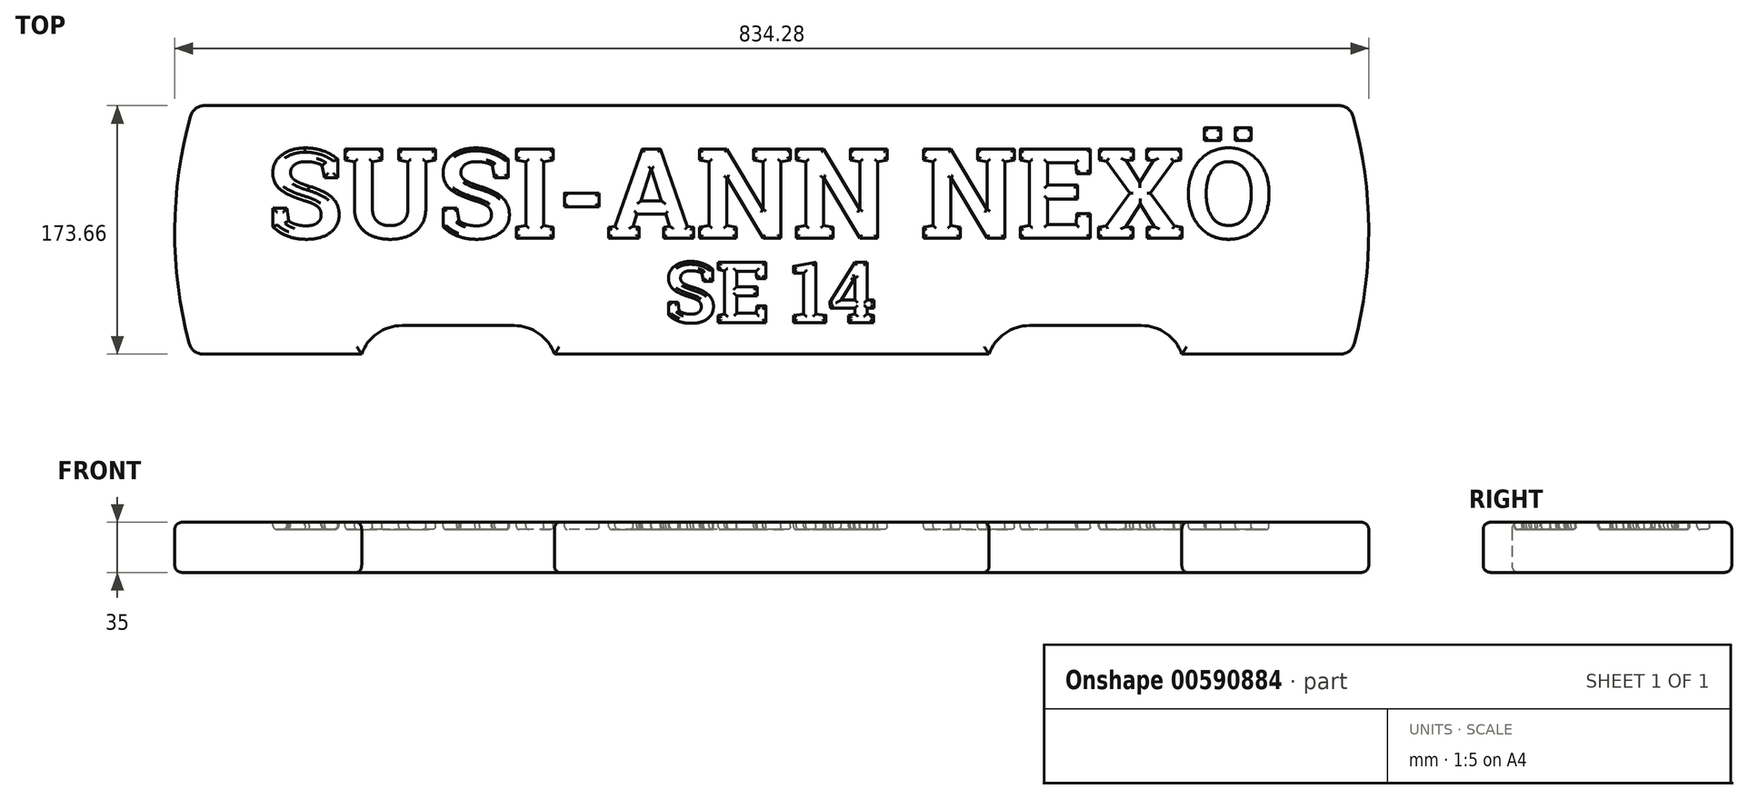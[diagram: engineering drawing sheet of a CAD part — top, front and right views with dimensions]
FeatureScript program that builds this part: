
annotation { "Feature Type Name" : "Feature", "Feature Type Description" : "" }
export const myFeature = defineFeature(function(context is Context, id is Id, definition is map)
    precondition{}
    {
        {
            var Q0;
            Q0=qCreatedBy(makeId("Top.planeOp"),FACE);
            var sketch = newSketch(context, id + "F0", { "sketchPlane" : qUnion([Q0])});
            skLineSegment(sketch, "E0.bottom", {"start": v(7.6, 0) * mm, "end": v(118.46, 0) * mm});
            skLineSegment(sketch, "E0.top", {"start": v(8.6, 173.66) * mm, "end": v(801.4, 173.66) * mm});
            skArc(sketch, "E1", {"start": v(-1.04, 166.34) * mm, "mid": v(-12.13, 86.96) * mm, "end": v(-2.07, 7.45) * mm});
            skLineSegment(sketch, "E2", {"start": v(405, 173.66) * mm, "end": v(405, 0) * mm, "construction": true});
            skArc(sketch, "E3.MirrorCS", {"start": v(811.04, 166.34) * mm, "mid": v(822.13, 86.96) * mm, "end": v(812.07, 7.45) * mm});
            skPoint(sketch, "E4.visualSharp", {"position": v(1.1, 173.66) * mm});
            skArc(sketch, "E4.filletArc", {"start": v(8.6, 173.66) * mm, "mid": v(2.54, 171.62) * mm, "end": v(-1.04, 166.34) * mm});
            skArc(sketch, "E5.MirrorCS", {"start": v(801.4, 173.66) * mm, "mid": v(807.46, 171.62) * mm, "end": v(811.04, 166.34) * mm});
            skPoint(sketch, "E6.orphan", {"position": v(808.9, 173.66) * mm});
            skLineSegment(sketch, "E7", {"start": v(-12.13, 86.9) * mm, "end": v(822.13, 86.9) * mm, "construction": true});
            skPoint(sketch, "E7.startSnap0", {"position": v(-12.13, 83.1) * mm});
            skPoint(sketch, "E8.visualSharp", {"position": v(0, 0) * mm});
            skArc(sketch, "E8.filletArc", {"start": v(-2.07, 7.45) * mm, "mid": v(1.5, 2.08) * mm, "end": v(7.6, 0) * mm});
            skPoint(sketch, "E9.visualSharp", {"position": v(810, 0) * mm});
            skArc(sketch, "E9.filletArc", {"start": v(802.4, 0) * mm, "mid": v(808.5, 2.08) * mm, "end": v(812.07, 7.45) * mm});
            skLineSegment(sketch, "E10.top", {"start": v(146.74, 20) * mm, "end": v(224.83, 20) * mm});
            skPoint(sketch, "E11.visualSharp", {"position": v(126.74, 20) * mm});
            skArc(sketch, "E11.filletArc", {"start": v(146.74, 20) * mm, "mid": v(129.42, 14.5) * mm, "end": v(118.46, 0) * mm});
            skPoint(sketch, "E12.visualSharp", {"position": v(244.83, 20) * mm});
            skArc(sketch, "E12.filletArc", {"start": v(253.12, 0) * mm, "mid": v(242.16, 14.5) * mm, "end": v(224.83, 20) * mm});
            skLineSegment(sketch, "E13.trimOffspring", {"start": v(253.12, 0) * mm, "end": v(556.88, 0) * mm});
            skArc(sketch, "E14.MirrorCS", {"start": v(556.88, 0) * mm, "mid": v(567.84, 14.5) * mm, "end": v(585.17, 20) * mm});
            skArc(sketch, "E15.MirrorCS", {"start": v(663.26, 20) * mm, "mid": v(680.58, 14.5) * mm, "end": v(691.54, 0) * mm});
            skPoint(sketch, "E16.MirrorP", {"position": v(565.17, 20) * mm});
            skPoint(sketch, "E17.MirrorP", {"position": v(683.26, 20) * mm});
            skLineSegment(sketch, "E18.MirrorCS", {"start": v(663.26, 20) * mm, "end": v(585.17, 20) * mm});
            skLineSegment(sketch, "E19.trimOffspring", {"start": v(691.54, 0) * mm, "end": v(802.4, 0) * mm});
            skSolve(sketch);
        }
        {
            var Q0;
            Q0 = qSketchRegion(id + "F0", true);
            extrude(context, id + "F1", {"entities" : qUnion([Q0]), "depth" : 35 * mm, "offsetDistance" : 25 * mm});
        }
        {
            var Q0;
            Q0=makeQuery(id+"F1.opExtrude","CAP_FACE",FACE,{"disambiguationData":[OSD([sQuery(id+"F0.wireOp",EDGE,"E0.bottom"),sQuery(id+"F0.wireOp",EDGE,"E0.top"),sQuery(id+"F0.wireOp",EDGE,"E1"),sQuery(id+"F0.wireOp",EDGE,"E3.MirrorCS"),sQuery(id+"F0.wireOp",EDGE,"E4.filletArc"),sQuery(id+"F0.wireOp",EDGE,"E5.MirrorCS"),sQuery(id+"F0.wireOp",EDGE,"E8.filletArc"),sQuery(id+"F0.wireOp",EDGE,"E9.filletArc"),sQuery(id+"F0.wireOp",EDGE,"E10.top"),sQuery(id+"F0.wireOp",EDGE,"E11.filletArc"),sQuery(id+"F0.wireOp",EDGE,"E12.filletArc"),sQuery(id+"F0.wireOp",EDGE,"E13.trimOffspring"),sQuery(id+"F0.wireOp",EDGE,"E14.MirrorCS"),sQuery(id+"F0.wireOp",EDGE,"E15.MirrorCS"),sQuery(id+"F0.wireOp",EDGE,"E18.MirrorCS"),sQuery(id+"F0.wireOp",EDGE,"E19.trimOffspring")])],"isStart":false});
            var Q1;
            Q1=makeQuery(id+"F1.opExtrude","CAP_FACE",FACE,{"disambiguationData":[OSD([sQuery(id+"F0.wireOp",EDGE,"E0.bottom"),sQuery(id+"F0.wireOp",EDGE,"E0.top"),sQuery(id+"F0.wireOp",EDGE,"E1"),sQuery(id+"F0.wireOp",EDGE,"E3.MirrorCS"),sQuery(id+"F0.wireOp",EDGE,"E4.filletArc"),sQuery(id+"F0.wireOp",EDGE,"E5.MirrorCS"),sQuery(id+"F0.wireOp",EDGE,"E8.filletArc"),sQuery(id+"F0.wireOp",EDGE,"E9.filletArc"),sQuery(id+"F0.wireOp",EDGE,"E10.top"),sQuery(id+"F0.wireOp",EDGE,"E11.filletArc"),sQuery(id+"F0.wireOp",EDGE,"E12.filletArc"),sQuery(id+"F0.wireOp",EDGE,"E13.trimOffspring"),sQuery(id+"F0.wireOp",EDGE,"E14.MirrorCS"),sQuery(id+"F0.wireOp",EDGE,"E15.MirrorCS"),sQuery(id+"F0.wireOp",EDGE,"E18.MirrorCS"),sQuery(id+"F0.wireOp",EDGE,"E19.trimOffspring")])],"isStart":true});
            fillet(context, id + "F2", {"entities" : qUnion([Q0, Q1]), "radius" : 5 * mm, "tangentPropagation" : true, "allowEdgeOverflow" : false});
        }
        {
            var Q0;
            Q0=makeQuery(id+"F1.opExtrude","CAP_FACE",FACE,{"disambiguationData":[OSD([sQuery(id+"F0.wireOp",EDGE,"E0.bottom"),sQuery(id+"F0.wireOp",EDGE,"E0.top"),sQuery(id+"F0.wireOp",EDGE,"E1"),sQuery(id+"F0.wireOp",EDGE,"E3.MirrorCS"),sQuery(id+"F0.wireOp",EDGE,"E4.filletArc"),sQuery(id+"F0.wireOp",EDGE,"E5.MirrorCS"),sQuery(id+"F0.wireOp",EDGE,"E8.filletArc"),sQuery(id+"F0.wireOp",EDGE,"E9.filletArc"),sQuery(id+"F0.wireOp",EDGE,"E10.top"),sQuery(id+"F0.wireOp",EDGE,"E11.filletArc"),sQuery(id+"F0.wireOp",EDGE,"E12.filletArc"),sQuery(id+"F0.wireOp",EDGE,"E13.trimOffspring"),sQuery(id+"F0.wireOp",EDGE,"E14.MirrorCS"),sQuery(id+"F0.wireOp",EDGE,"E15.MirrorCS"),sQuery(id+"F0.wireOp",EDGE,"E18.MirrorCS"),sQuery(id+"F0.wireOp",EDGE,"E19.trimOffspring")])],"isStart":false});
            var sketch = newSketch(context, id + "F3", { "sketchPlane" : qUnion([Q0])});
            skText(sketch, "E20", { "text": "SUSI-ANN NEXÖ", "fontName": "RobotoSlab-Bold.ttf"});
            skLineSegment(sketch, "E21", {"start": v(405, 168.66) * mm, "end": v(405, 5) * mm, "construction": true});
            skText(sketch, "E22", { "text": "SE 14", "fontName": "RobotoSlab-Bold.ttf"});
            const initialGuessF3  = {"E20": [0.05221, 0.08113, 1, 0, 0.06292], "E22": [0.33004, 0.02212, 1, 0, 0.04265]};
            skSetInitialGuess(sketch, initialGuessF3);
            skSolve(sketch);
        }
        {
            var Q0;
            Q0 = qSketchRegion(id + "F3", true);
            extrude(context, id + "F4", {"entities" : qUnion([Q0]), "operationType" : NewBodyOperationType.REMOVE, "oppositeDirection" : true, "depth" : 5 * mm, "offsetDistance" : 25 * mm});
        }
        {
            var Q0;
            Q0=makeQuery(id+"F4.boolean.opBoolean","COPY",FACE,{"derivedFrom":makeQuery(id+"F4.opExtrude","CAP_FACE",FACE,{"disambiguationData":[OSD([sQuery(id+"F3.wireOp",EDGE,"E20.sketch_text.stroke-0"),sQuery(id+"F3.wireOp",EDGE,"E20.sketch_text.stroke-1"),sQuery(id+"F3.wireOp",EDGE,"E20.sketch_text.stroke-2"),sQuery(id+"F3.wireOp",EDGE,"E20.sketch_text.stroke-3"),sQuery(id+"F3.wireOp",EDGE,"E20.sketch_text.stroke-4"),sQuery(id+"F3.wireOp",EDGE,"E20.sketch_text.stroke-5"),sQuery(id+"F3.wireOp",EDGE,"E20.sketch_text.stroke-6"),sQuery(id+"F3.wireOp",EDGE,"E20.sketch_text.stroke-7"),sQuery(id+"F3.wireOp",EDGE,"E20.sketch_text.stroke-8"),sQuery(id+"F3.wireOp",EDGE,"E20.sketch_text.stroke-9"),sQuery(id+"F3.wireOp",EDGE,"E20.sketch_text.stroke-10"),sQuery(id+"F3.wireOp",EDGE,"E20.sketch_text.stroke-11"),sQuery(id+"F3.wireOp",EDGE,"E20.sketch_text.stroke-12"),sQuery(id+"F3.wireOp",EDGE,"E20.sketch_text.stroke-13"),sQuery(id+"F3.wireOp",EDGE,"E20.sketch_text.stroke-14"),sQuery(id+"F3.wireOp",EDGE,"E20.sketch_text.stroke-15"),sQuery(id+"F3.wireOp",EDGE,"E20.sketch_text.stroke-16"),sQuery(id+"F3.wireOp",EDGE,"E20.sketch_text.stroke-17"),sQuery(id+"F3.wireOp",EDGE,"E20.sketch_text.stroke-18"),sQuery(id+"F3.wireOp",EDGE,"E20.sketch_text.stroke-19"),sQuery(id+"F3.wireOp",EDGE,"E20.sketch_text.stroke-20"),sQuery(id+"F3.wireOp",EDGE,"E20.sketch_text.stroke-21"),sQuery(id+"F3.wireOp",EDGE,"E20.sketch_text.stroke-22"),sQuery(id+"F3.wireOp",EDGE,"E20.sketch_text.stroke-23"),sQuery(id+"F3.wireOp",EDGE,"E20.sketch_text.stroke-24"),sQuery(id+"F3.wireOp",EDGE,"E20.sketch_text.stroke-25"),sQuery(id+"F3.wireOp",EDGE,"E20.sketch_text.stroke-26"),sQuery(id+"F3.wireOp",EDGE,"E20.sketch_text.stroke-27"),sQuery(id+"F3.wireOp",EDGE,"E20.sketch_text.stroke-28"),sQuery(id+"F3.wireOp",EDGE,"E20.sketch_text.stroke-29")])],"isStart":false})});
            fillet(context, id + "F5", {"entities" : qUnion([Q0]), "radius" : 3 * mm, "tangentPropagation" : true, "allowEdgeOverflow" : false});
        }
        {
            var Q0;
            Q0=makeQuery(id+"F4.boolean.opBoolean","COPY",FACE,{"derivedFrom":makeQuery(id+"F4.opExtrude","CAP_FACE",FACE,{"disambiguationData":[OSD([sQuery(id+"F3.wireOp",EDGE,"E20.sketch_text.stroke-30"),sQuery(id+"F3.wireOp",EDGE,"E20.sketch_text.stroke-31"),sQuery(id+"F3.wireOp",EDGE,"E20.sketch_text.stroke-32"),sQuery(id+"F3.wireOp",EDGE,"E20.sketch_text.stroke-33"),sQuery(id+"F3.wireOp",EDGE,"E20.sketch_text.stroke-34"),sQuery(id+"F3.wireOp",EDGE,"E20.sketch_text.stroke-35"),sQuery(id+"F3.wireOp",EDGE,"E20.sketch_text.stroke-36"),sQuery(id+"F3.wireOp",EDGE,"E20.sketch_text.stroke-37"),sQuery(id+"F3.wireOp",EDGE,"E20.sketch_text.stroke-38"),sQuery(id+"F3.wireOp",EDGE,"E20.sketch_text.stroke-39"),sQuery(id+"F3.wireOp",EDGE,"E20.sketch_text.stroke-40"),sQuery(id+"F3.wireOp",EDGE,"E20.sketch_text.stroke-41"),sQuery(id+"F3.wireOp",EDGE,"E20.sketch_text.stroke-42"),sQuery(id+"F3.wireOp",EDGE,"E20.sketch_text.stroke-43"),sQuery(id+"F3.wireOp",EDGE,"E20.sketch_text.stroke-44"),sQuery(id+"F3.wireOp",EDGE,"E20.sketch_text.stroke-45"),sQuery(id+"F3.wireOp",EDGE,"E20.sketch_text.stroke-46"),sQuery(id+"F3.wireOp",EDGE,"E20.sketch_text.stroke-47"),sQuery(id+"F3.wireOp",EDGE,"E20.sketch_text.stroke-48"),sQuery(id+"F3.wireOp",EDGE,"E20.sketch_text.stroke-49"),sQuery(id+"F3.wireOp",EDGE,"E20.sketch_text.stroke-50"),sQuery(id+"F3.wireOp",EDGE,"E20.sketch_text.stroke-51"),sQuery(id+"F3.wireOp",EDGE,"E20.sketch_text.stroke-52"),sQuery(id+"F3.wireOp",EDGE,"E20.sketch_text.stroke-53")])],"isStart":false})});
            var Q1;
            Q1=makeQuery(id+"F4.boolean.opBoolean","COPY",FACE,{"derivedFrom":makeQuery(id+"F4.opExtrude","CAP_FACE",FACE,{"disambiguationData":[OSD([sQuery(id+"F3.wireOp",EDGE,"E20.sketch_text.stroke-54"),sQuery(id+"F3.wireOp",EDGE,"E20.sketch_text.stroke-55"),sQuery(id+"F3.wireOp",EDGE,"E20.sketch_text.stroke-56"),sQuery(id+"F3.wireOp",EDGE,"E20.sketch_text.stroke-57"),sQuery(id+"F3.wireOp",EDGE,"E20.sketch_text.stroke-58"),sQuery(id+"F3.wireOp",EDGE,"E20.sketch_text.stroke-59"),sQuery(id+"F3.wireOp",EDGE,"E20.sketch_text.stroke-60"),sQuery(id+"F3.wireOp",EDGE,"E20.sketch_text.stroke-61"),sQuery(id+"F3.wireOp",EDGE,"E20.sketch_text.stroke-62"),sQuery(id+"F3.wireOp",EDGE,"E20.sketch_text.stroke-63"),sQuery(id+"F3.wireOp",EDGE,"E20.sketch_text.stroke-64"),sQuery(id+"F3.wireOp",EDGE,"E20.sketch_text.stroke-65"),sQuery(id+"F3.wireOp",EDGE,"E20.sketch_text.stroke-66"),sQuery(id+"F3.wireOp",EDGE,"E20.sketch_text.stroke-67"),sQuery(id+"F3.wireOp",EDGE,"E20.sketch_text.stroke-68"),sQuery(id+"F3.wireOp",EDGE,"E20.sketch_text.stroke-69"),sQuery(id+"F3.wireOp",EDGE,"E20.sketch_text.stroke-70"),sQuery(id+"F3.wireOp",EDGE,"E20.sketch_text.stroke-71"),sQuery(id+"F3.wireOp",EDGE,"E20.sketch_text.stroke-72"),sQuery(id+"F3.wireOp",EDGE,"E20.sketch_text.stroke-73"),sQuery(id+"F3.wireOp",EDGE,"E20.sketch_text.stroke-74"),sQuery(id+"F3.wireOp",EDGE,"E20.sketch_text.stroke-75"),sQuery(id+"F3.wireOp",EDGE,"E20.sketch_text.stroke-76"),sQuery(id+"F3.wireOp",EDGE,"E20.sketch_text.stroke-77"),sQuery(id+"F3.wireOp",EDGE,"E20.sketch_text.stroke-78"),sQuery(id+"F3.wireOp",EDGE,"E20.sketch_text.stroke-79"),sQuery(id+"F3.wireOp",EDGE,"E20.sketch_text.stroke-80"),sQuery(id+"F3.wireOp",EDGE,"E20.sketch_text.stroke-81"),sQuery(id+"F3.wireOp",EDGE,"E20.sketch_text.stroke-82"),sQuery(id+"F3.wireOp",EDGE,"E20.sketch_text.stroke-83")])],"isStart":false})});
            var Q2;
            Q2=makeQuery(id+"F4.boolean.opBoolean","COPY",FACE,{"derivedFrom":makeQuery(id+"F4.opExtrude","CAP_FACE",FACE,{"disambiguationData":[OSD([sQuery(id+"F3.wireOp",EDGE,"E20.sketch_text.stroke-84"),sQuery(id+"F3.wireOp",EDGE,"E20.sketch_text.stroke-85"),sQuery(id+"F3.wireOp",EDGE,"E20.sketch_text.stroke-86"),sQuery(id+"F3.wireOp",EDGE,"E20.sketch_text.stroke-87"),sQuery(id+"F3.wireOp",EDGE,"E20.sketch_text.stroke-88"),sQuery(id+"F3.wireOp",EDGE,"E20.sketch_text.stroke-89"),sQuery(id+"F3.wireOp",EDGE,"E20.sketch_text.stroke-90"),sQuery(id+"F3.wireOp",EDGE,"E20.sketch_text.stroke-91"),sQuery(id+"F3.wireOp",EDGE,"E20.sketch_text.stroke-92"),sQuery(id+"F3.wireOp",EDGE,"E20.sketch_text.stroke-93"),sQuery(id+"F3.wireOp",EDGE,"E20.sketch_text.stroke-94"),sQuery(id+"F3.wireOp",EDGE,"E20.sketch_text.stroke-95")])],"isStart":false})});
            var Q3;
            Q3=makeQuery(id+"F4.boolean.opBoolean","COPY",FACE,{"derivedFrom":makeQuery(id+"F4.opExtrude","CAP_FACE",FACE,{"disambiguationData":[OSD([sQuery(id+"F3.wireOp",EDGE,"E20.sketch_text.stroke-96"),sQuery(id+"F3.wireOp",EDGE,"E20.sketch_text.stroke-97"),sQuery(id+"F3.wireOp",EDGE,"E20.sketch_text.stroke-98"),sQuery(id+"F3.wireOp",EDGE,"E20.sketch_text.stroke-99")])],"isStart":false})});
            var Q4;
            Q4=makeQuery(id+"F4.boolean.opBoolean","COPY",FACE,{"derivedFrom":makeQuery(id+"F4.opExtrude","CAP_FACE",FACE,{"disambiguationData":[OSD([sQuery(id+"F3.wireOp",EDGE,"E20.sketch_text.stroke-100"),sQuery(id+"F3.wireOp",EDGE,"E20.sketch_text.stroke-101"),sQuery(id+"F3.wireOp",EDGE,"E20.sketch_text.stroke-102"),sQuery(id+"F3.wireOp",EDGE,"E20.sketch_text.stroke-103"),sQuery(id+"F3.wireOp",EDGE,"E20.sketch_text.stroke-104"),sQuery(id+"F3.wireOp",EDGE,"E20.sketch_text.stroke-105"),sQuery(id+"F3.wireOp",EDGE,"E20.sketch_text.stroke-106"),sQuery(id+"F3.wireOp",EDGE,"E20.sketch_text.stroke-107"),sQuery(id+"F3.wireOp",EDGE,"E20.sketch_text.stroke-108"),sQuery(id+"F3.wireOp",EDGE,"E20.sketch_text.stroke-109"),sQuery(id+"F3.wireOp",EDGE,"E20.sketch_text.stroke-110"),sQuery(id+"F3.wireOp",EDGE,"E20.sketch_text.stroke-111"),sQuery(id+"F3.wireOp",EDGE,"E20.sketch_text.stroke-112"),sQuery(id+"F3.wireOp",EDGE,"E20.sketch_text.stroke-113"),sQuery(id+"F3.wireOp",EDGE,"E20.sketch_text.stroke-114"),sQuery(id+"F3.wireOp",EDGE,"E20.sketch_text.stroke-115"),sQuery(id+"F3.wireOp",EDGE,"E20.sketch_text.stroke-116"),sQuery(id+"F3.wireOp",EDGE,"E20.sketch_text.stroke-117"),sQuery(id+"F3.wireOp",EDGE,"E20.sketch_text.stroke-118"),sQuery(id+"F3.wireOp",EDGE,"E20.sketch_text.stroke-119")])],"isStart":false})});
            var Q5;
            Q5=makeQuery(id+"F4.boolean.opBoolean","COPY",FACE,{"derivedFrom":makeQuery(id+"F4.opExtrude","CAP_FACE",FACE,{"disambiguationData":[OSD([sQuery(id+"F3.wireOp",EDGE,"E20.sketch_text.stroke-120"),sQuery(id+"F3.wireOp",EDGE,"E20.sketch_text.stroke-121"),sQuery(id+"F3.wireOp",EDGE,"E20.sketch_text.stroke-122"),sQuery(id+"F3.wireOp",EDGE,"E20.sketch_text.stroke-123"),sQuery(id+"F3.wireOp",EDGE,"E20.sketch_text.stroke-124"),sQuery(id+"F3.wireOp",EDGE,"E20.sketch_text.stroke-125"),sQuery(id+"F3.wireOp",EDGE,"E20.sketch_text.stroke-126"),sQuery(id+"F3.wireOp",EDGE,"E20.sketch_text.stroke-127"),sQuery(id+"F3.wireOp",EDGE,"E20.sketch_text.stroke-128"),sQuery(id+"F3.wireOp",EDGE,"E20.sketch_text.stroke-129"),sQuery(id+"F3.wireOp",EDGE,"E20.sketch_text.stroke-130"),sQuery(id+"F3.wireOp",EDGE,"E20.sketch_text.stroke-131"),sQuery(id+"F3.wireOp",EDGE,"E20.sketch_text.stroke-132"),sQuery(id+"F3.wireOp",EDGE,"E20.sketch_text.stroke-133"),sQuery(id+"F3.wireOp",EDGE,"E20.sketch_text.stroke-134"),sQuery(id+"F3.wireOp",EDGE,"E20.sketch_text.stroke-135"),sQuery(id+"F3.wireOp",EDGE,"E20.sketch_text.stroke-136"),sQuery(id+"F3.wireOp",EDGE,"E20.sketch_text.stroke-137"),sQuery(id+"F3.wireOp",EDGE,"E20.sketch_text.stroke-138"),sQuery(id+"F3.wireOp",EDGE,"E20.sketch_text.stroke-139"),sQuery(id+"F3.wireOp",EDGE,"E20.sketch_text.stroke-140"),sQuery(id+"F3.wireOp",EDGE,"E20.sketch_text.stroke-141"),sQuery(id+"F3.wireOp",EDGE,"E20.sketch_text.stroke-142"),sQuery(id+"F3.wireOp",EDGE,"E20.sketch_text.stroke-143")])],"isStart":false})});
            var Q6;
            Q6=makeQuery(id+"F4.boolean.opBoolean","COPY",FACE,{"derivedFrom":makeQuery(id+"F4.opExtrude","CAP_FACE",FACE,{"disambiguationData":[OSD([sQuery(id+"F3.wireOp",EDGE,"E20.sketch_text.stroke-144"),sQuery(id+"F3.wireOp",EDGE,"E20.sketch_text.stroke-145"),sQuery(id+"F3.wireOp",EDGE,"E20.sketch_text.stroke-146"),sQuery(id+"F3.wireOp",EDGE,"E20.sketch_text.stroke-147"),sQuery(id+"F3.wireOp",EDGE,"E20.sketch_text.stroke-148"),sQuery(id+"F3.wireOp",EDGE,"E20.sketch_text.stroke-149"),sQuery(id+"F3.wireOp",EDGE,"E20.sketch_text.stroke-150"),sQuery(id+"F3.wireOp",EDGE,"E20.sketch_text.stroke-151"),sQuery(id+"F3.wireOp",EDGE,"E20.sketch_text.stroke-152"),sQuery(id+"F3.wireOp",EDGE,"E20.sketch_text.stroke-153"),sQuery(id+"F3.wireOp",EDGE,"E20.sketch_text.stroke-154"),sQuery(id+"F3.wireOp",EDGE,"E20.sketch_text.stroke-155"),sQuery(id+"F3.wireOp",EDGE,"E20.sketch_text.stroke-156"),sQuery(id+"F3.wireOp",EDGE,"E20.sketch_text.stroke-157"),sQuery(id+"F3.wireOp",EDGE,"E20.sketch_text.stroke-158"),sQuery(id+"F3.wireOp",EDGE,"E20.sketch_text.stroke-159"),sQuery(id+"F3.wireOp",EDGE,"E20.sketch_text.stroke-160"),sQuery(id+"F3.wireOp",EDGE,"E20.sketch_text.stroke-161"),sQuery(id+"F3.wireOp",EDGE,"E20.sketch_text.stroke-162"),sQuery(id+"F3.wireOp",EDGE,"E20.sketch_text.stroke-163"),sQuery(id+"F3.wireOp",EDGE,"E20.sketch_text.stroke-164"),sQuery(id+"F3.wireOp",EDGE,"E20.sketch_text.stroke-165"),sQuery(id+"F3.wireOp",EDGE,"E20.sketch_text.stroke-166"),sQuery(id+"F3.wireOp",EDGE,"E20.sketch_text.stroke-167")])],"isStart":false})});
            var Q7;
            Q7=makeQuery(id+"F4.boolean.opBoolean","COPY",FACE,{"derivedFrom":makeQuery(id+"F4.opExtrude","CAP_FACE",FACE,{"disambiguationData":[OSD([sQuery(id+"F3.wireOp",EDGE,"E20.sketch_text.stroke-168"),sQuery(id+"F3.wireOp",EDGE,"E20.sketch_text.stroke-169"),sQuery(id+"F3.wireOp",EDGE,"E20.sketch_text.stroke-170"),sQuery(id+"F3.wireOp",EDGE,"E20.sketch_text.stroke-171"),sQuery(id+"F3.wireOp",EDGE,"E20.sketch_text.stroke-172"),sQuery(id+"F3.wireOp",EDGE,"E20.sketch_text.stroke-173"),sQuery(id+"F3.wireOp",EDGE,"E20.sketch_text.stroke-174"),sQuery(id+"F3.wireOp",EDGE,"E20.sketch_text.stroke-175"),sQuery(id+"F3.wireOp",EDGE,"E20.sketch_text.stroke-176"),sQuery(id+"F3.wireOp",EDGE,"E20.sketch_text.stroke-177"),sQuery(id+"F3.wireOp",EDGE,"E20.sketch_text.stroke-178"),sQuery(id+"F3.wireOp",EDGE,"E20.sketch_text.stroke-179"),sQuery(id+"F3.wireOp",EDGE,"E20.sketch_text.stroke-180"),sQuery(id+"F3.wireOp",EDGE,"E20.sketch_text.stroke-181"),sQuery(id+"F3.wireOp",EDGE,"E20.sketch_text.stroke-182"),sQuery(id+"F3.wireOp",EDGE,"E20.sketch_text.stroke-183"),sQuery(id+"F3.wireOp",EDGE,"E20.sketch_text.stroke-184"),sQuery(id+"F3.wireOp",EDGE,"E20.sketch_text.stroke-185"),sQuery(id+"F3.wireOp",EDGE,"E20.sketch_text.stroke-186"),sQuery(id+"F3.wireOp",EDGE,"E20.sketch_text.stroke-187"),sQuery(id+"F3.wireOp",EDGE,"E20.sketch_text.stroke-188"),sQuery(id+"F3.wireOp",EDGE,"E20.sketch_text.stroke-189"),sQuery(id+"F3.wireOp",EDGE,"E20.sketch_text.stroke-190"),sQuery(id+"F3.wireOp",EDGE,"E20.sketch_text.stroke-191")])],"isStart":false})});
            var Q8;
            Q8=makeQuery(id+"F4.boolean.opBoolean","COPY",FACE,{"derivedFrom":makeQuery(id+"F4.opExtrude","CAP_FACE",FACE,{"disambiguationData":[OSD([sQuery(id+"F3.wireOp",EDGE,"E20.sketch_text.stroke-192"),sQuery(id+"F3.wireOp",EDGE,"E20.sketch_text.stroke-193"),sQuery(id+"F3.wireOp",EDGE,"E20.sketch_text.stroke-194"),sQuery(id+"F3.wireOp",EDGE,"E20.sketch_text.stroke-195"),sQuery(id+"F3.wireOp",EDGE,"E20.sketch_text.stroke-196"),sQuery(id+"F3.wireOp",EDGE,"E20.sketch_text.stroke-197"),sQuery(id+"F3.wireOp",EDGE,"E20.sketch_text.stroke-198"),sQuery(id+"F3.wireOp",EDGE,"E20.sketch_text.stroke-199"),sQuery(id+"F3.wireOp",EDGE,"E20.sketch_text.stroke-200"),sQuery(id+"F3.wireOp",EDGE,"E20.sketch_text.stroke-201"),sQuery(id+"F3.wireOp",EDGE,"E20.sketch_text.stroke-202"),sQuery(id+"F3.wireOp",EDGE,"E20.sketch_text.stroke-203"),sQuery(id+"F3.wireOp",EDGE,"E20.sketch_text.stroke-204"),sQuery(id+"F3.wireOp",EDGE,"E20.sketch_text.stroke-205"),sQuery(id+"F3.wireOp",EDGE,"E20.sketch_text.stroke-206"),sQuery(id+"F3.wireOp",EDGE,"E20.sketch_text.stroke-207"),sQuery(id+"F3.wireOp",EDGE,"E20.sketch_text.stroke-208"),sQuery(id+"F3.wireOp",EDGE,"E20.sketch_text.stroke-209"),sQuery(id+"F3.wireOp",EDGE,"E20.sketch_text.stroke-210"),sQuery(id+"F3.wireOp",EDGE,"E20.sketch_text.stroke-211"),sQuery(id+"F3.wireOp",EDGE,"E20.sketch_text.stroke-212")])],"isStart":false})});
            var Q9;
            Q9=makeQuery(id+"F4.boolean.opBoolean","COPY",FACE,{"derivedFrom":makeQuery(id+"F4.opExtrude","CAP_FACE",FACE,{"disambiguationData":[OSD([sQuery(id+"F3.wireOp",EDGE,"E20.sketch_text.stroke-213"),sQuery(id+"F3.wireOp",EDGE,"E20.sketch_text.stroke-214"),sQuery(id+"F3.wireOp",EDGE,"E20.sketch_text.stroke-215"),sQuery(id+"F3.wireOp",EDGE,"E20.sketch_text.stroke-216"),sQuery(id+"F3.wireOp",EDGE,"E20.sketch_text.stroke-217"),sQuery(id+"F3.wireOp",EDGE,"E20.sketch_text.stroke-218"),sQuery(id+"F3.wireOp",EDGE,"E20.sketch_text.stroke-219"),sQuery(id+"F3.wireOp",EDGE,"E20.sketch_text.stroke-220"),sQuery(id+"F3.wireOp",EDGE,"E20.sketch_text.stroke-221"),sQuery(id+"F3.wireOp",EDGE,"E20.sketch_text.stroke-222"),sQuery(id+"F3.wireOp",EDGE,"E20.sketch_text.stroke-223"),sQuery(id+"F3.wireOp",EDGE,"E20.sketch_text.stroke-224"),sQuery(id+"F3.wireOp",EDGE,"E20.sketch_text.stroke-225"),sQuery(id+"F3.wireOp",EDGE,"E20.sketch_text.stroke-226"),sQuery(id+"F3.wireOp",EDGE,"E20.sketch_text.stroke-227"),sQuery(id+"F3.wireOp",EDGE,"E20.sketch_text.stroke-228"),sQuery(id+"F3.wireOp",EDGE,"E20.sketch_text.stroke-229"),sQuery(id+"F3.wireOp",EDGE,"E20.sketch_text.stroke-230"),sQuery(id+"F3.wireOp",EDGE,"E20.sketch_text.stroke-231"),sQuery(id+"F3.wireOp",EDGE,"E20.sketch_text.stroke-232"),sQuery(id+"F3.wireOp",EDGE,"E20.sketch_text.stroke-233"),sQuery(id+"F3.wireOp",EDGE,"E20.sketch_text.stroke-234"),sQuery(id+"F3.wireOp",EDGE,"E20.sketch_text.stroke-235"),sQuery(id+"F3.wireOp",EDGE,"E20.sketch_text.stroke-236"),sQuery(id+"F3.wireOp",EDGE,"E20.sketch_text.stroke-237"),sQuery(id+"F3.wireOp",EDGE,"E20.sketch_text.stroke-238"),sQuery(id+"F3.wireOp",EDGE,"E20.sketch_text.stroke-239"),sQuery(id+"F3.wireOp",EDGE,"E20.sketch_text.stroke-240")])],"isStart":false})});
            var Q10;
            Q10=makeQuery(id+"F4.boolean.opBoolean","COPY",FACE,{"derivedFrom":makeQuery(id+"F4.opExtrude","CAP_FACE",FACE,{"disambiguationData":[OSD([sQuery(id+"F3.wireOp",EDGE,"E20.sketch_text.stroke-241"),sQuery(id+"F3.wireOp",EDGE,"E20.sketch_text.stroke-242"),sQuery(id+"F3.wireOp",EDGE,"E20.sketch_text.stroke-243"),sQuery(id+"F3.wireOp",EDGE,"E20.sketch_text.stroke-244"),sQuery(id+"F3.wireOp",EDGE,"E20.sketch_text.stroke-245"),sQuery(id+"F3.wireOp",EDGE,"E20.sketch_text.stroke-246"),sQuery(id+"F3.wireOp",EDGE,"E20.sketch_text.stroke-247"),sQuery(id+"F3.wireOp",EDGE,"E20.sketch_text.stroke-248"),sQuery(id+"F3.wireOp",EDGE,"E20.sketch_text.stroke-249"),sQuery(id+"F3.wireOp",EDGE,"E20.sketch_text.stroke-250"),sQuery(id+"F3.wireOp",EDGE,"E20.sketch_text.stroke-251"),sQuery(id+"F3.wireOp",EDGE,"E20.sketch_text.stroke-252"),sQuery(id+"F3.wireOp",EDGE,"E20.sketch_text.stroke-253"),sQuery(id+"F3.wireOp",EDGE,"E20.sketch_text.stroke-254"),sQuery(id+"F3.wireOp",EDGE,"E20.sketch_text.stroke-255"),sQuery(id+"F3.wireOp",EDGE,"E20.sketch_text.stroke-256"),sQuery(id+"F3.wireOp",EDGE,"E20.sketch_text.stroke-257"),sQuery(id+"F3.wireOp",EDGE,"E20.sketch_text.stroke-258"),sQuery(id+"F3.wireOp",EDGE,"E20.sketch_text.stroke-259"),sQuery(id+"F3.wireOp",EDGE,"E20.sketch_text.stroke-260")])],"isStart":false})});
            var Q11;
            Q11=makeQuery(id+"F4.boolean.opBoolean","COPY",FACE,{"derivedFrom":makeQuery(id+"F4.opExtrude","CAP_FACE",FACE,{"disambiguationData":[OSD([sQuery(id+"F3.wireOp",EDGE,"E20.sketch_text.stroke-265"),sQuery(id+"F3.wireOp",EDGE,"E20.sketch_text.stroke-266"),sQuery(id+"F3.wireOp",EDGE,"E20.sketch_text.stroke-267"),sQuery(id+"F3.wireOp",EDGE,"E20.sketch_text.stroke-268")])],"isStart":false})});
            var Q12;
            Q12=makeQuery(id+"F4.boolean.opBoolean","COPY",FACE,{"derivedFrom":makeQuery(id+"F4.opExtrude","CAP_FACE",FACE,{"disambiguationData":[OSD([sQuery(id+"F3.wireOp",EDGE,"E20.sketch_text.stroke-261"),sQuery(id+"F3.wireOp",EDGE,"E20.sketch_text.stroke-262"),sQuery(id+"F3.wireOp",EDGE,"E20.sketch_text.stroke-263"),sQuery(id+"F3.wireOp",EDGE,"E20.sketch_text.stroke-264")])],"isStart":false})});
            var Q13;
            Q13=makeQuery(id+"F4.boolean.opBoolean","COPY",FACE,{"derivedFrom":makeQuery(id+"F4.opExtrude","CAP_FACE",FACE,{"disambiguationData":[OSD([sQuery(id+"F3.wireOp",EDGE,"E22.sketch_text.stroke-61"),sQuery(id+"F3.wireOp",EDGE,"E22.sketch_text.stroke-62"),sQuery(id+"F3.wireOp",EDGE,"E22.sketch_text.stroke-63"),sQuery(id+"F3.wireOp",EDGE,"E22.sketch_text.stroke-64"),sQuery(id+"F3.wireOp",EDGE,"E22.sketch_text.stroke-65"),sQuery(id+"F3.wireOp",EDGE,"E22.sketch_text.stroke-66"),sQuery(id+"F3.wireOp",EDGE,"E22.sketch_text.stroke-67"),sQuery(id+"F3.wireOp",EDGE,"E22.sketch_text.stroke-68"),sQuery(id+"F3.wireOp",EDGE,"E22.sketch_text.stroke-69"),sQuery(id+"F3.wireOp",EDGE,"E22.sketch_text.stroke-70"),sQuery(id+"F3.wireOp",EDGE,"E22.sketch_text.stroke-71"),sQuery(id+"F3.wireOp",EDGE,"E22.sketch_text.stroke-72"),sQuery(id+"F3.wireOp",EDGE,"E22.sketch_text.stroke-73"),sQuery(id+"F3.wireOp",EDGE,"E22.sketch_text.stroke-74"),sQuery(id+"F3.wireOp",EDGE,"E22.sketch_text.stroke-75"),sQuery(id+"F3.wireOp",EDGE,"E22.sketch_text.stroke-76"),sQuery(id+"F3.wireOp",EDGE,"E22.sketch_text.stroke-77"),sQuery(id+"F3.wireOp",EDGE,"E22.sketch_text.stroke-78"),sQuery(id+"F3.wireOp",EDGE,"E22.sketch_text.stroke-79"),sQuery(id+"F3.wireOp",EDGE,"E22.sketch_text.stroke-80")])],"isStart":false})});
            var Q14;
            Q14=makeQuery(id+"F4.boolean.opBoolean","COPY",FACE,{"derivedFrom":makeQuery(id+"F4.opExtrude","CAP_FACE",FACE,{"disambiguationData":[OSD([sQuery(id+"F3.wireOp",EDGE,"E22.sketch_text.stroke-51"),sQuery(id+"F3.wireOp",EDGE,"E22.sketch_text.stroke-52"),sQuery(id+"F3.wireOp",EDGE,"E22.sketch_text.stroke-53"),sQuery(id+"F3.wireOp",EDGE,"E22.sketch_text.stroke-54"),sQuery(id+"F3.wireOp",EDGE,"E22.sketch_text.stroke-55"),sQuery(id+"F3.wireOp",EDGE,"E22.sketch_text.stroke-56"),sQuery(id+"F3.wireOp",EDGE,"E22.sketch_text.stroke-57"),sQuery(id+"F3.wireOp",EDGE,"E22.sketch_text.stroke-58"),sQuery(id+"F3.wireOp",EDGE,"E22.sketch_text.stroke-59"),sQuery(id+"F3.wireOp",EDGE,"E22.sketch_text.stroke-60")])],"isStart":false})});
            var Q15;
            Q15=makeQuery(id+"F4.boolean.opBoolean","COPY",FACE,{"derivedFrom":makeQuery(id+"F4.opExtrude","CAP_FACE",FACE,{"disambiguationData":[OSD([sQuery(id+"F3.wireOp",EDGE,"E22.sketch_text.stroke-30"),sQuery(id+"F3.wireOp",EDGE,"E22.sketch_text.stroke-31"),sQuery(id+"F3.wireOp",EDGE,"E22.sketch_text.stroke-32"),sQuery(id+"F3.wireOp",EDGE,"E22.sketch_text.stroke-33"),sQuery(id+"F3.wireOp",EDGE,"E22.sketch_text.stroke-34"),sQuery(id+"F3.wireOp",EDGE,"E22.sketch_text.stroke-35"),sQuery(id+"F3.wireOp",EDGE,"E22.sketch_text.stroke-36"),sQuery(id+"F3.wireOp",EDGE,"E22.sketch_text.stroke-37"),sQuery(id+"F3.wireOp",EDGE,"E22.sketch_text.stroke-38"),sQuery(id+"F3.wireOp",EDGE,"E22.sketch_text.stroke-39"),sQuery(id+"F3.wireOp",EDGE,"E22.sketch_text.stroke-40"),sQuery(id+"F3.wireOp",EDGE,"E22.sketch_text.stroke-41"),sQuery(id+"F3.wireOp",EDGE,"E22.sketch_text.stroke-42"),sQuery(id+"F3.wireOp",EDGE,"E22.sketch_text.stroke-43"),sQuery(id+"F3.wireOp",EDGE,"E22.sketch_text.stroke-44"),sQuery(id+"F3.wireOp",EDGE,"E22.sketch_text.stroke-45"),sQuery(id+"F3.wireOp",EDGE,"E22.sketch_text.stroke-46"),sQuery(id+"F3.wireOp",EDGE,"E22.sketch_text.stroke-47"),sQuery(id+"F3.wireOp",EDGE,"E22.sketch_text.stroke-48"),sQuery(id+"F3.wireOp",EDGE,"E22.sketch_text.stroke-49"),sQuery(id+"F3.wireOp",EDGE,"E22.sketch_text.stroke-50")])],"isStart":false})});
            var Q16;
            Q16=makeQuery(id+"F4.boolean.opBoolean","COPY",FACE,{"derivedFrom":makeQuery(id+"F4.opExtrude","CAP_FACE",FACE,{"disambiguationData":[OSD([sQuery(id+"F3.wireOp",EDGE,"E22.sketch_text.stroke-0"),sQuery(id+"F3.wireOp",EDGE,"E22.sketch_text.stroke-1"),sQuery(id+"F3.wireOp",EDGE,"E22.sketch_text.stroke-2"),sQuery(id+"F3.wireOp",EDGE,"E22.sketch_text.stroke-3"),sQuery(id+"F3.wireOp",EDGE,"E22.sketch_text.stroke-4"),sQuery(id+"F3.wireOp",EDGE,"E22.sketch_text.stroke-5"),sQuery(id+"F3.wireOp",EDGE,"E22.sketch_text.stroke-6"),sQuery(id+"F3.wireOp",EDGE,"E22.sketch_text.stroke-7"),sQuery(id+"F3.wireOp",EDGE,"E22.sketch_text.stroke-8"),sQuery(id+"F3.wireOp",EDGE,"E22.sketch_text.stroke-9"),sQuery(id+"F3.wireOp",EDGE,"E22.sketch_text.stroke-10"),sQuery(id+"F3.wireOp",EDGE,"E22.sketch_text.stroke-11"),sQuery(id+"F3.wireOp",EDGE,"E22.sketch_text.stroke-12"),sQuery(id+"F3.wireOp",EDGE,"E22.sketch_text.stroke-13"),sQuery(id+"F3.wireOp",EDGE,"E22.sketch_text.stroke-14"),sQuery(id+"F3.wireOp",EDGE,"E22.sketch_text.stroke-15"),sQuery(id+"F3.wireOp",EDGE,"E22.sketch_text.stroke-16"),sQuery(id+"F3.wireOp",EDGE,"E22.sketch_text.stroke-17"),sQuery(id+"F3.wireOp",EDGE,"E22.sketch_text.stroke-18"),sQuery(id+"F3.wireOp",EDGE,"E22.sketch_text.stroke-19"),sQuery(id+"F3.wireOp",EDGE,"E22.sketch_text.stroke-20"),sQuery(id+"F3.wireOp",EDGE,"E22.sketch_text.stroke-21"),sQuery(id+"F3.wireOp",EDGE,"E22.sketch_text.stroke-22"),sQuery(id+"F3.wireOp",EDGE,"E22.sketch_text.stroke-23"),sQuery(id+"F3.wireOp",EDGE,"E22.sketch_text.stroke-24"),sQuery(id+"F3.wireOp",EDGE,"E22.sketch_text.stroke-25"),sQuery(id+"F3.wireOp",EDGE,"E22.sketch_text.stroke-26"),sQuery(id+"F3.wireOp",EDGE,"E22.sketch_text.stroke-27"),sQuery(id+"F3.wireOp",EDGE,"E22.sketch_text.stroke-28"),sQuery(id+"F3.wireOp",EDGE,"E22.sketch_text.stroke-29")])],"isStart":false})});
            fillet(context, id + "F6", {"entities" : qUnion([Q0, Q1, Q2, Q3, Q4, Q5, Q6, Q7, Q8, Q9, Q10, Q11, Q12, Q13, Q14, Q15, Q16]), "radius" : 2 * mm, "tangentPropagation" : true, "allowEdgeOverflow" : false});
        }
    });
